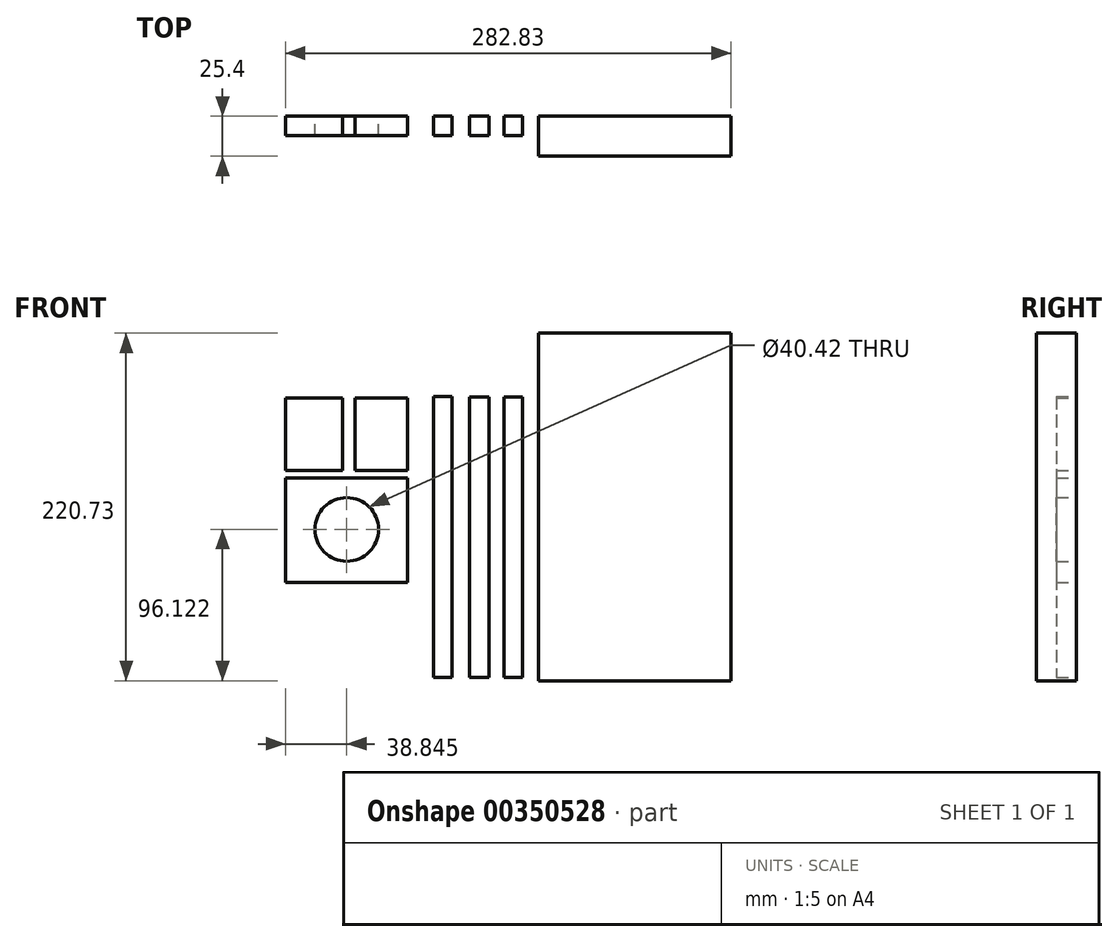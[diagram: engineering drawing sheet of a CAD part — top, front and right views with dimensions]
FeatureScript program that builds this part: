
annotation { "Feature Type Name" : "Feature", "Feature Type Description" : "" }
export const myFeature = defineFeature(function(context is Context, id is Id, definition is map)
    precondition{}
    {
        {
            var Q0;
            Q0=qCreatedBy(makeId("Front.planeOp"),FACE);
            var sketch = newSketch(context, id + "F0", { "sketchPlane" : qUnion([Q0])});
            skLineSegment(sketch, "E0.bottom", {"start": v(-47.36, 60.3) * mm, "end": v(-14.06, 60.3) * mm});
            skLineSegment(sketch, "E0.top", {"start": v(-47.36, 14.06) * mm, "end": v(-14.06, 14.06) * mm});
            skLineSegment(sketch, "E0.left", {"start": v(-47.36, 60.3) * mm, "end": v(-47.36, 14.06) * mm});
            skLineSegment(sketch, "E0.right", {"start": v(-14.06, 60.3) * mm, "end": v(-14.06, 14.06) * mm});
            skLineSegment(sketch, "E1.bottom", {"start": v(2.59, 61.04) * mm, "end": v(14.43, 61.04) * mm});
            skLineSegment(sketch, "E1.top", {"start": v(2.59, -117.28) * mm, "end": v(14.43, -117.28) * mm});
            skLineSegment(sketch, "E1.left", {"start": v(2.59, 61.04) * mm, "end": v(2.59, -117.28) * mm});
            skLineSegment(sketch, "E1.right", {"start": v(14.43, 61.04) * mm, "end": v(14.43, -117.28) * mm});
            skLineSegment(sketch, "E2.bottom", {"start": v(25.53, 60.67) * mm, "end": v(37.74, 60.67) * mm});
            skLineSegment(sketch, "E2.top", {"start": v(25.53, -117.28) * mm, "end": v(37.74, -117.28) * mm});
            skLineSegment(sketch, "E2.left", {"start": v(25.53, 60.67) * mm, "end": v(25.53, -117.28) * mm});
            skLineSegment(sketch, "E2.right", {"start": v(37.74, 60.67) * mm, "end": v(37.74, -117.28) * mm});
            skLineSegment(sketch, "E3.bottom", {"start": v(47.36, 60.67) * mm, "end": v(59.2, 60.67) * mm});
            skLineSegment(sketch, "E3.top", {"start": v(47.36, -117.28) * mm, "end": v(59.2, -117.28) * mm});
            skLineSegment(sketch, "E3.left", {"start": v(47.36, 60.67) * mm, "end": v(47.36, -117.28) * mm});
            skLineSegment(sketch, "E3.right", {"start": v(59.2, 60.67) * mm, "end": v(59.2, -117.28) * mm});
            skLineSegment(sketch, "E4.bottom", {"start": v(-91.38, 9.25) * mm, "end": v(-14.06, 9.25) * mm});
            skLineSegment(sketch, "E4.top", {"start": v(-91.38, -56.97) * mm, "end": v(-14.06, -56.97) * mm});
            skLineSegment(sketch, "E4.left", {"start": v(-91.38, 9.25) * mm, "end": v(-91.38, -56.97) * mm});
            skLineSegment(sketch, "E4.right", {"start": v(-14.06, 9.25) * mm, "end": v(-14.06, -56.97) * mm});
            skCircle(sketch, "E5", {"center": v(-52.54, -23.3) * mm, "radius": 20.2 * mm});
            skLineSegment(sketch, "E6.bottom", {"start": v(-55.12, 14.06) * mm, "end": v(-91.38, 14.06) * mm});
            skLineSegment(sketch, "E6.top", {"start": v(-55.12, 60.3) * mm, "end": v(-91.38, 60.3) * mm});
            skLineSegment(sketch, "E6.left", {"start": v(-55.12, 14.06) * mm, "end": v(-55.12, 60.3) * mm});
            skLineSegment(sketch, "E6.right", {"start": v(-91.38, 14.06) * mm, "end": v(-91.38, 60.3) * mm});
            skLineSegment(sketch, "E7.bottom", {"start": v(69.15, 101.3) * mm, "end": v(191.45, 101.3) * mm});
            skLineSegment(sketch, "E7.top", {"start": v(69.15, -119.43) * mm, "end": v(191.45, -119.43) * mm});
            skLineSegment(sketch, "E7.left", {"start": v(69.15, 101.3) * mm, "end": v(69.15, -119.43) * mm});
            skLineSegment(sketch, "E7.right", {"start": v(191.45, 101.3) * mm, "end": v(191.45, -119.43) * mm});
            skSolve(sketch);
        }
        {
            var Q0;
            Q0=makeQuery(id+"F0.imprint","IMPRINT",FACE,{"disambiguationData":[TD([[makeQuery(id+"F0.imprint","IMPRINT",EDGE,{"derivedFrom":sQuery(id+"F0.wireOp",EDGE,"E6.bottom")}),-1.0]])]});
            var Q1;
            Q1=makeQuery(id+"F0.imprint","IMPRINT",FACE,{"disambiguationData":[TD([[makeQuery(id+"F0.imprint","IMPRINT",EDGE,{"derivedFrom":sQuery(id+"F0.wireOp",EDGE,"E0.bottom")}),-1.0]])]});
            var Q2;
            Q2=makeQuery(id+"F0.imprint","IMPRINT",FACE,{"disambiguationData":[TD([[makeQuery(id+"F0.imprint","IMPRINT",EDGE,{"derivedFrom":sQuery(id+"F0.wireOp",EDGE,"E1.bottom")}),-1.0]])]});
            var Q3;
            Q3=makeQuery(id+"F0.imprint","IMPRINT",FACE,{"disambiguationData":[TD([[makeQuery(id+"F0.imprint","IMPRINT",EDGE,{"derivedFrom":sQuery(id+"F0.wireOp",EDGE,"E2.bottom")}),-1.0]])]});
            var Q4;
            Q4=makeQuery(id+"F0.imprint","IMPRINT",FACE,{"disambiguationData":[TD([[makeQuery(id+"F0.imprint","IMPRINT",EDGE,{"derivedFrom":sQuery(id+"F0.wireOp",EDGE,"E3.bottom")}),-1.0]])]});
            var Q5;
            Q5=makeQuery(id+"F0.imprint","IMPRINT",FACE,{"disambiguationData":[TD([[makeQuery(id+"F0.imprint","IMPRINT",EDGE,{"derivedFrom":sQuery(id+"F0.wireOp",EDGE,"E4.bottom")}),-1.0]])]});
            extrude(context, id + "F1", {"entities" : qUnion([Q0, Q1, Q2, Q3, Q4, Q5]), "depth" : 12.45 * mm});
        }
        {
            var Q0;
            Q0=makeQuery(id+"F0.imprint","IMPRINT",FACE,{"disambiguationData":[TD([[makeQuery(id+"F0.imprint","IMPRINT",EDGE,{"derivedFrom":sQuery(id+"F0.wireOp",EDGE,"E7.bottom")}),-1.0]])]});
            extrude(context, id + "F2", {"entities" : qUnion([Q0]), "depth" : 25.4 * mm});
        }
    });
